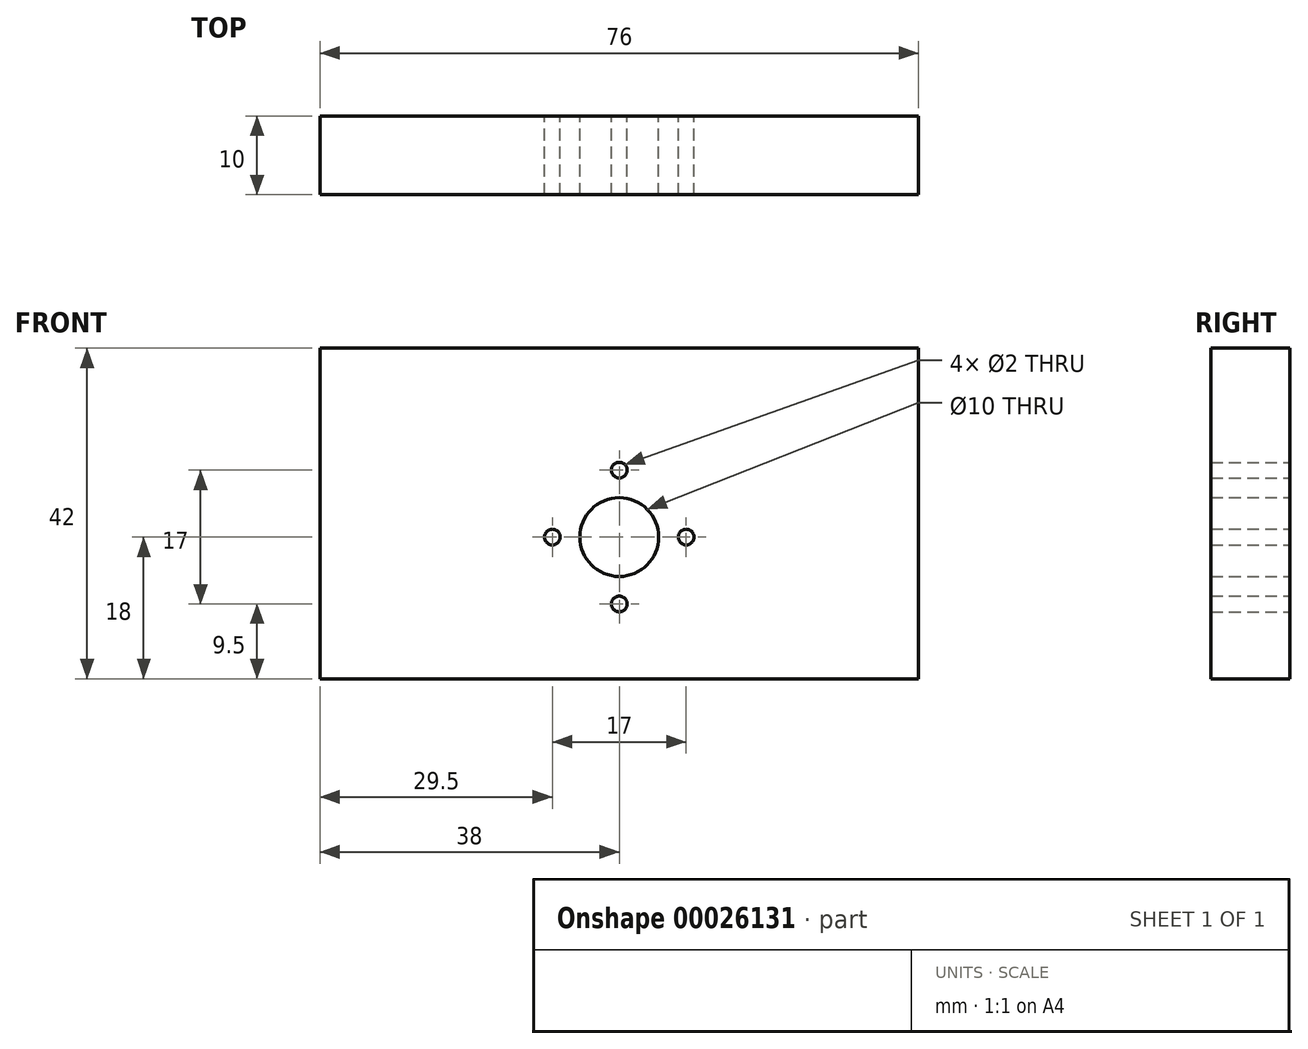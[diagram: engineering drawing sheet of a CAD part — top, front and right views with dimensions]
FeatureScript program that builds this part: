
annotation { "Feature Type Name" : "Feature", "Feature Type Description" : "" }
export const myFeature = defineFeature(function(context is Context, id is Id, definition is map)
    precondition{}
    {
        {
            var Q0;
            Q0=qCreatedBy(makeId("Front.planeOp"),FACE);
            var sketch = newSketch(context, id + "F0", { "sketchPlane" : qUnion([Q0])});
            skLineSegment(sketch, "E0.rect.bottom", {"start": v(-38, -21) * mm, "end": v(38, -21) * mm});
            skLineSegment(sketch, "E0.rect.top", {"start": v(-38, 21) * mm, "end": v(38, 21) * mm});
            skLineSegment(sketch, "E0.rect.left", {"start": v(-38, -21) * mm, "end": v(-38, 21) * mm});
            skLineSegment(sketch, "E0.rect.right", {"start": v(38, -21) * mm, "end": v(38, 21) * mm});
            skPoint(sketch, "E0.rect.middle", {"position": v(0, 0) * mm});
            skLineSegment(sketch, "E1", {"start": v(-38, 11) * mm, "end": v(38, 11) * mm, "construction": true});
            skCircle(sketch, "E2", {"center": v(0, -3) * mm, "radius": 5 * mm});
            skLineSegment(sketch, "E3", {"start": v(-8.5, -3) * mm, "end": v(8.5, -3) * mm, "construction": true});
            skCircle(sketch, "E4", {"center": v(-8.5, -3) * mm, "radius": 1 * mm});
            skCircle(sketch, "E5", {"center": v(8.5, -3) * mm, "radius": 1 * mm});
            skLineSegment(sketch, "E6", {"start": v(0, -11.5) * mm, "end": v(0, 5.5) * mm, "construction": true});
            skCircle(sketch, "E7", {"center": v(0, 5.5) * mm, "radius": 1 * mm});
            skCircle(sketch, "E8", {"center": v(0, -11.5) * mm, "radius": 1 * mm});
            skPoint(sketch, "E9", {"position": v(0, -8) * mm});
            skLineSegment(sketch, "E10", {"start": v(-38, -8) * mm, "end": v(38, -8) * mm, "construction": true});
            skSolve(sketch);
        }
        {
            var Q0;
            Q0=makeQuery(id+"F0.imprint","IMPRINT",FACE,{"disambiguationData":[TD([[makeQuery(id+"F0.imprint","IMPRINT",EDGE,{"derivedFrom":sQuery(id+"F0.wireOp",EDGE,"E0.rect.bottom")}),1.0]])]});
            extrude(context, id + "F1", {"entities" : qUnion([Q0]), "endBound" : BoundingType.SYMMETRIC, "depth" : 10 * mm});
        }
    });
